# Revit family: Lighting_Fixture-Wall-Astro-Teetoo
name_source: partatom
category: Lighting Fixtures
revit_build: Autodesk Revit 2014 (Build: 20130308_1515(x64)
units: mm (PartAtom-declared; Revit-internal decimal feet)

## types (6) — shared parameters
Assembly Code = D5020200
Class = 1
Color Filter = 16777215
Description = Wall Light
Dimmable = Yes
Dimming Lamp Color Temperature Shift = <None>
Energy Efficiency Rating = - C
Height = 50 mm  [stored 0.164042 ft]
IP Rating = IP20
Lamp = G4
Lamp included = Yes
Length = 180 mm  [stored 0.590551 ft]
Light Source Elevation = 1600 mm  [stored 5.24934 ft]
Light Source From Wall = 170 mm  [stored 0.557743 ft]
Luminaire Lamp Efficiency Rating = - A-C
Manufacturer = Astro Lighting Ltd, CM20 2DP
Mountable on normally flammable surfaces = Yes
Number of Poles = 1
Suitable for bathroom zone = Zone 3
Tilt Angle = 90.00°
Type Comments = Includes integral transformer
URL = www.astrolighting.co.uk
Voltage = 230 V

## per-type parameters (varying)
| type | Apparent Load | Casing Material | Model | Photometric Web File | Product Documentation | Wattage Comments | Weight | Width |
| 0793 Teetoo 350 (12v) (Chrome) | 43 VA | Astro - Steel - Chrome Finish | 0793 Teetoo 350 (12v) Chrome | 0793 TEETOO 350 12V POLISHED CHROME.ies | http://www.astrolighting.co.uk
/kw/0793/0793_Teetoo-350-(12v) | 2x20W | 0.9 kg | 350 mm  [stored 1.14829 ft] |
| 0796 Teetoo 550 (12v) (Chrome) | 48 VA | Astro - Steel - Chrome Finish | 0796 Teetoo 550 (12v) Chrome | 0796 TEETOO 550 12V POLISHED CHROME.ies | http://www.astrolighting.co.uk
/kw/0796/0796_Teetoo-550-(12v) | 4x10W | 1.2 kg | 550 mm |
| 0794 Teetoo 350 (12v) (Matt Nickel) | 43 VA | Astro - Steel - Matt Nickel | 0794 Teetoo 350 (12v) Matt Nickel | 0793 TEETOO 350 12V POLISHED CHROME.ies | http://www.astrolighting.co.uk
/kw/0793/0793_Teetoo-350-(12v) | 2x20W | 0.9 kg | 350 mm  [stored 1.14829 ft] |
| 0795 Teetoo 350 (12v) (Bronze) | 43 VA | Astro - Steel - Bronze | 0795 Teetoo 350 (12v) Bronze | 0793 TEETOO 350 12V POLISHED CHROME.ies | http://www.astrolighting.co.uk
/kw/0793/0793_Teetoo-350-(12v) | 2x20W | 0.9 kg | 350 mm  [stored 1.14829 ft] |
| 0797 Teetoo 550 (12v) (Matt Nickel) | 48 VA | Astro - Steel - Matt Nickel | 0797 Teetoo 550 (12v) Matt Nickel | 0796 TEETOO 550 12V POLISHED CHROME.ies | http://www.astrolighting.co.uk
/kw/0796/0796_Teetoo-550-(12v) | 4x10W | 1.2 kg | 550 mm |
| 0798 Teetoo 550 (12v) (Bronze) | 48 VA | Astro - Steel - Bronze | 0798 Teetoo 550 (12v) Bronze | 0796 TEETOO 550 12V POLISHED CHROME.ies | http://www.astrolighting.co.uk
/kw/0796/0796_Teetoo-550-(12v) | 4x10W | 1.2 kg | 550 mm |

note: [stored X ft] marks values corroborated as IEEE doubles in the binary element streams (Revit-internal decimal feet)

## geometry (parser evidence)
native form markers: Sweep x2
no freeform markers — native parametric forms only
